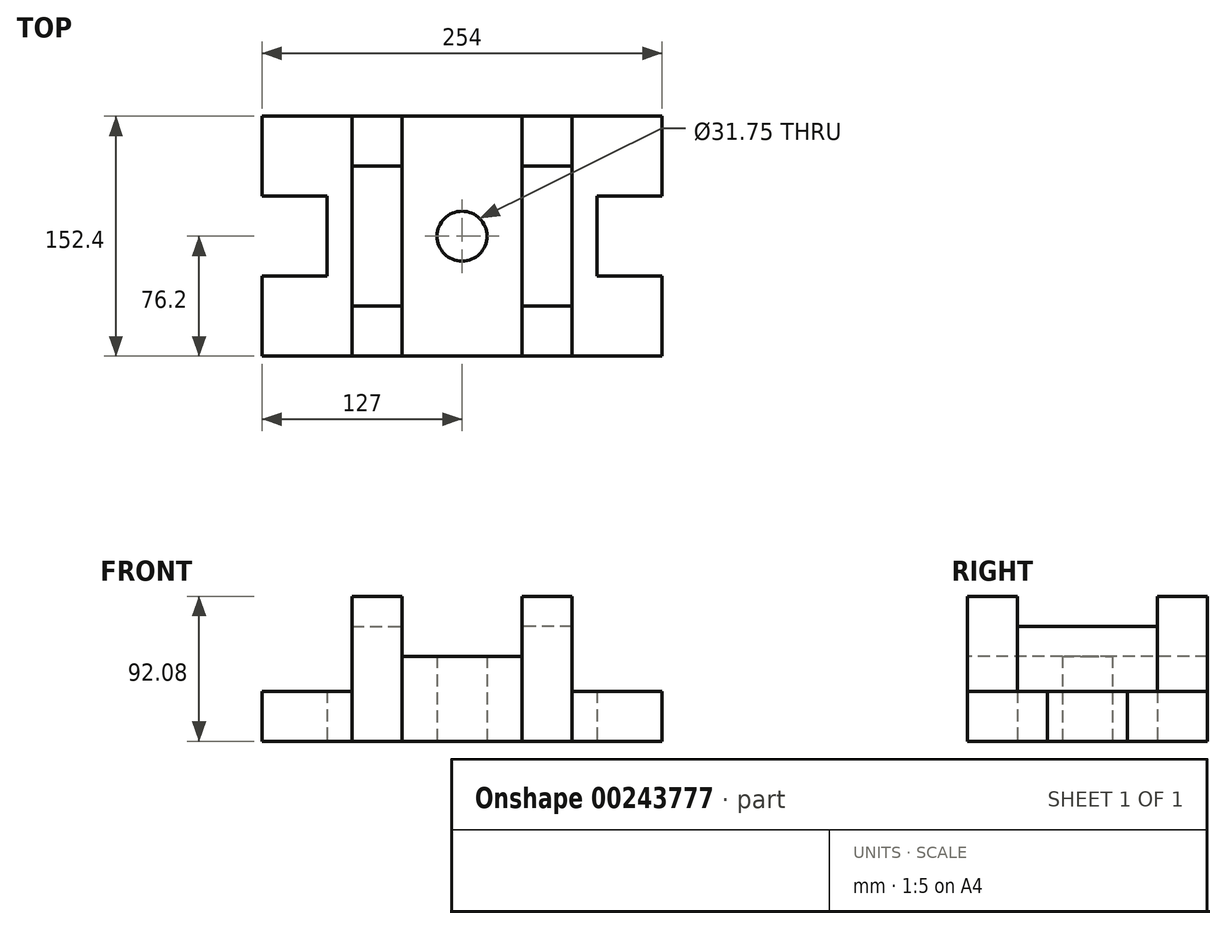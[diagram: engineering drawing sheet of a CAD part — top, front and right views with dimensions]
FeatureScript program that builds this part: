
annotation { "Feature Type Name" : "Feature", "Feature Type Description" : "" }
export const myFeature = defineFeature(function(context is Context, id is Id, definition is map)
    precondition{}
    {
        {
            var Q0;
            Q0=qCreatedBy(makeId("Top.planeOp"),FACE);
            var sketch = newSketch(context, id + "F0", { "sketchPlane" : qUnion([Q0])});
            skCircle(sketch, "E0", {"center": v(0, 0) * mm, "radius": 15.88 * mm});
            skLineSegment(sketch, "E1", {"start": v(-38.1, -76.2) * mm, "end": v(38.1, -76.2) * mm});
            skLineSegment(sketch, "E2.MirrorCS", {"start": v(-38.1, 76.2) * mm, "end": v(38.1, 76.2) * mm});
            skLineSegment(sketch, "E3", {"start": v(-38.1, 76.2) * mm, "end": v(-38.1, -76.2) * mm});
            skLineSegment(sketch, "E4", {"start": v(38.1, 76.2) * mm, "end": v(38.1, -76.2) * mm});
            skLineSegment(sketch, "E5", {"start": v(38.1, -76.2) * mm, "end": v(69.85, -76.2) * mm});
            skLineSegment(sketch, "E6", {"start": v(69.85, -76.2) * mm, "end": v(69.85, -44.45) * mm});
            skLineSegment(sketch, "E7", {"start": v(69.85, -44.45) * mm, "end": v(69.85, 44.45) * mm});
            skLineSegment(sketch, "E8", {"start": v(69.85, 44.45) * mm, "end": v(69.85, 76.2) * mm});
            skLineSegment(sketch, "E9", {"start": v(69.85, 76.2) * mm, "end": v(38.1, 76.2) * mm});
            skLineSegment(sketch, "E10", {"start": v(69.85, -44.45) * mm, "end": v(38.1, -44.45) * mm});
            skLineSegment(sketch, "E11", {"start": v(69.85, 44.45) * mm, "end": v(38.1, 44.45) * mm});
            skPoint(sketch, "E12.endSnap0", {"position": v(0, -76.2) * mm});
            skLineSegment(sketch, "E13.MirrorCS", {"start": v(-69.85, 44.45) * mm, "end": v(-38.1, 44.45) * mm});
            skLineSegment(sketch, "E14.MirrorCS", {"start": v(-69.85, 76.2) * mm, "end": v(-38.1, 76.2) * mm});
            skLineSegment(sketch, "E15.MirrorCS", {"start": v(-69.85, 44.45) * mm, "end": v(-69.85, 76.2) * mm});
            skLineSegment(sketch, "E16.MirrorCS", {"start": v(-69.85, -44.45) * mm, "end": v(-69.85, 44.45) * mm});
            skLineSegment(sketch, "E17.MirrorCS", {"start": v(-69.85, -44.45) * mm, "end": v(-38.1, -44.45) * mm});
            skLineSegment(sketch, "E18.MirrorCS", {"start": v(-69.85, -76.2) * mm, "end": v(-69.85, -44.45) * mm});
            skLineSegment(sketch, "E19.MirrorCS", {"start": v(-38.1, -76.2) * mm, "end": v(-69.85, -76.2) * mm});
            skLineSegment(sketch, "E20", {"start": v(69.85, -76.2) * mm, "end": v(127, -76.2) * mm});
            skLineSegment(sketch, "E21", {"start": v(127, -76.2) * mm, "end": v(127, -25.4) * mm});
            skLineSegment(sketch, "E22", {"start": v(127, -25.4) * mm, "end": v(85.72, -25.4) * mm});
            skLineSegment(sketch, "E23", {"start": v(85.72, -25.4) * mm, "end": v(85.72, 25.4) * mm});
            skLineSegment(sketch, "E24", {"start": v(85.72, 25.4) * mm, "end": v(127, 25.4) * mm});
            skLineSegment(sketch, "E25", {"start": v(127, 25.4) * mm, "end": v(127, 76.2) * mm});
            skLineSegment(sketch, "E26", {"start": v(127, 76.2) * mm, "end": v(69.85, 76.2) * mm});
            skLineSegment(sketch, "E27.MirrorCS", {"start": v(-127, 76.2) * mm, "end": v(-69.85, 76.2) * mm});
            skLineSegment(sketch, "E28.MirrorCS", {"start": v(-127, 25.4) * mm, "end": v(-127, 76.2) * mm});
            skLineSegment(sketch, "E29.MirrorCS", {"start": v(-85.72, 25.4) * mm, "end": v(-127, 25.4) * mm});
            skLineSegment(sketch, "E30.MirrorCS", {"start": v(-85.72, -25.4) * mm, "end": v(-85.72, 25.4) * mm});
            skLineSegment(sketch, "E31.MirrorCS", {"start": v(-127, -25.4) * mm, "end": v(-85.72, -25.4) * mm});
            skLineSegment(sketch, "E32.MirrorCS", {"start": v(-127, -76.2) * mm, "end": v(-127, -25.4) * mm});
            skLineSegment(sketch, "E33.MirrorCS", {"start": v(-69.85, -76.2) * mm, "end": v(-127, -76.2) * mm});
            skSolve(sketch);
        }
        {
            var Q0;
            Q0=makeQuery(id+"F0.imprint","IMPRINT",FACE,{"disambiguationData":[TD([[makeQuery(id+"F0.imprint","IMPRINT",EDGE,{"derivedFrom":sQuery(id+"F0.wireOp",EDGE,"E15.MirrorCS")}),1.0]])]});
            var Q1;
            Q1=makeQuery(id+"F0.imprint","IMPRINT",FACE,{"disambiguationData":[TD([[makeQuery(id+"F0.imprint","IMPRINT",EDGE,{"derivedFrom":sQuery(id+"F0.wireOp",EDGE,"E6")}),-1.0]])]});
            extrude(context, id + "F1", {"entities" : qUnion([Q0, Q1]), "depth" : 31.75 * mm});
        }
        {
            var Q0;
            {var subQ0=sQuery(id+"F0.wireOp",EDGE,"E13.MirrorCS");Q0=makeQuery(id+"F0.imprint","IMPRINT",FACE,{"disambiguationData":[TD([[makeQuery(id+"F0.imprint","IMPRINT",EDGE,{"derivedFrom":subQ0}),-1.0]])]});}
            var Q1;
            Q1=makeQuery(id+"F0.imprint","IMPRINT",FACE,{"disambiguationData":[TD([[makeQuery(id+"F0.imprint","IMPRINT",EDGE,{"derivedFrom":sQuery(id+"F0.wireOp",EDGE,"E7")}),1.0]])]});
            extrude(context, id + "F2", {"entities" : qUnion([Q0, Q1]), "depth" : 73.02 * mm});
        }
        {
            var Q0;
            {var subQ2=sQuery(id+"F0.wireOp",EDGE,"E13.MirrorCS");Q0=makeQuery(id+"F0.imprint","IMPRINT",FACE,{"disambiguationData":[TD([[makeQuery(id+"F0.imprint","IMPRINT",EDGE,{"derivedFrom":subQ2}),1.0]])]});}
            var Q1;
            {var subQ2=sQuery(id+"F0.wireOp",EDGE,"E17.MirrorCS");Q1=makeQuery(id+"F0.imprint","IMPRINT",FACE,{"disambiguationData":[TD([[makeQuery(id+"F0.imprint","IMPRINT",EDGE,{"derivedFrom":subQ2}),-1.0]])]});}
            var Q2;
            Q2=makeQuery(id+"F0.imprint","IMPRINT",FACE,{"disambiguationData":[TD([[makeQuery(id+"F0.imprint","IMPRINT",EDGE,{"derivedFrom":sQuery(id+"F0.wireOp",EDGE,"E8")}),1.0]])]});
            var Q3;
            {var subQ0=sQuery(id+"F0.wireOp",EDGE,"E5");Q3=makeQuery(id+"F0.imprint","IMPRINT",FACE,{"disambiguationData":[TD([[makeQuery(id+"F0.imprint","IMPRINT",EDGE,{"derivedFrom":subQ0}),1.0]])]});}
            extrude(context, id + "F3", {"entities" : qUnion([Q0, Q1, Q2, Q3]), "depth" : 92.07 * mm});
        }
        {
            var Q0;
            Q0=makeQuery(id+"F0.imprint","IMPRINT",FACE,{"disambiguationData":[TD([[makeQuery(id+"F0.imprint","IMPRINT",EDGE,{"derivedFrom":sQuery(id+"F0.wireOp",EDGE,"E0")}),-1.0]])]});
            extrude(context, id + "F4", {"entities" : qUnion([Q0]), "depth" : 53.97 * mm});
        }
    });
